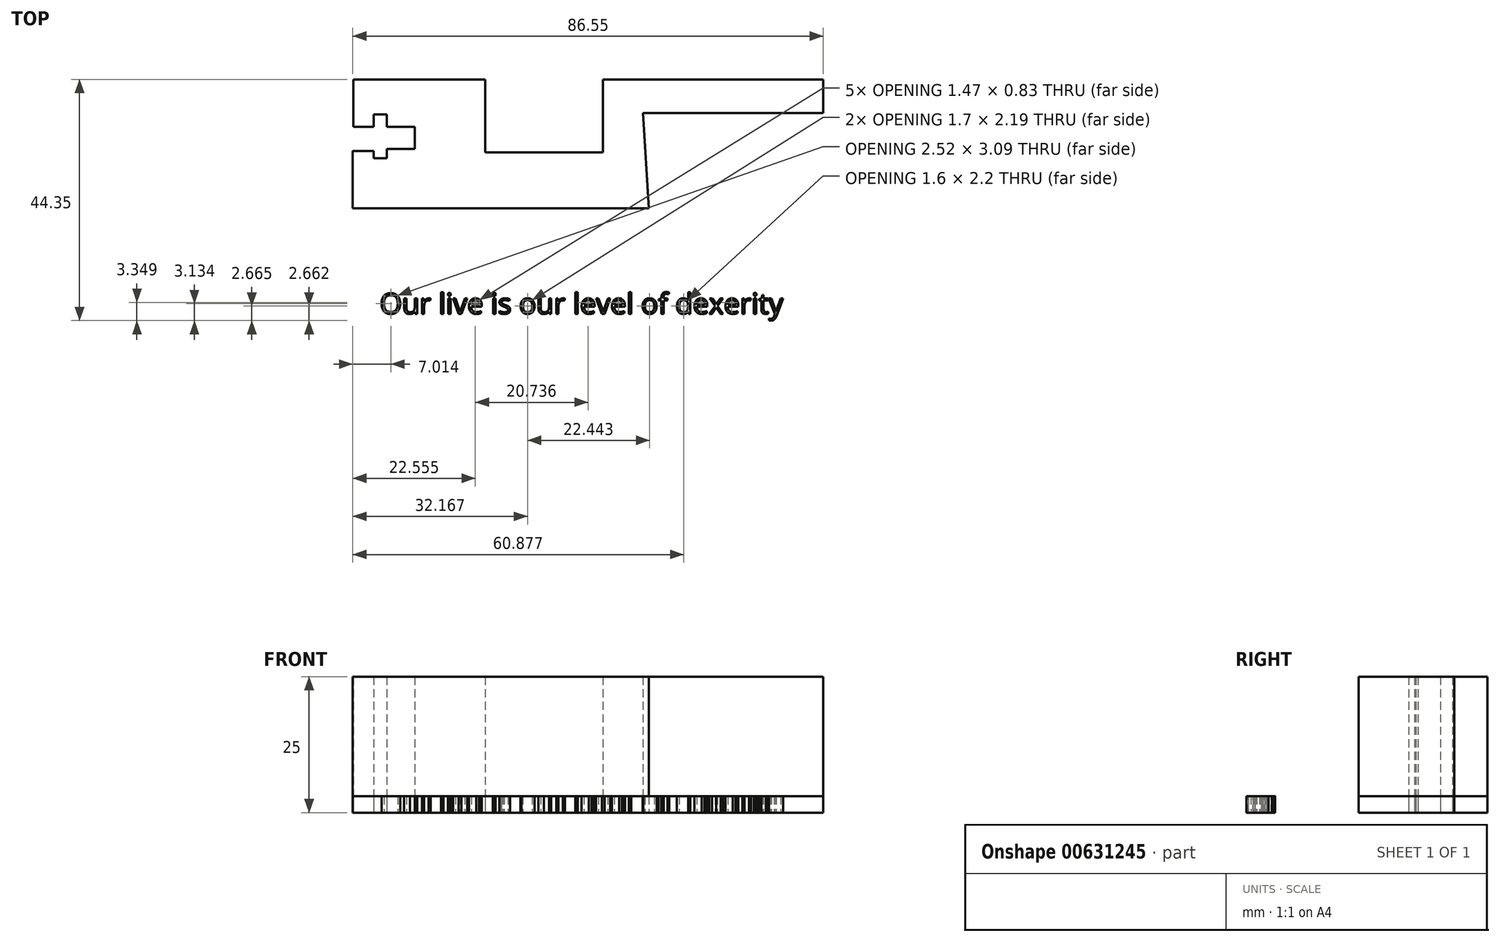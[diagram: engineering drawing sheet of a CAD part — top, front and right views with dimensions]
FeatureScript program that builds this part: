
annotation { "Feature Type Name" : "Feature", "Feature Type Description" : "" }
export const myFeature = defineFeature(function(context is Context, id is Id, definition is map)
    precondition{}
    {
        {
            var Q0;
            Q0=qCreatedBy(makeId("Top.planeOp"),FACE);
            var sketch = newSketch(context, id + "F0", { "sketchPlane" : qUnion([Q0])});
            skLineSegment(sketch, "E0", {"start": v(-137.92, 48.65) * mm, "end": v(-113.6, 48.65) * mm});
            skLineSegment(sketch, "E1", {"start": v(-113.6, 48.65) * mm, "end": v(-113.6, 35.24) * mm});
            skLineSegment(sketch, "E2", {"start": v(-113.6, 35.24) * mm, "end": v(-91.97, 35.24) * mm});
            skLineSegment(sketch, "E3", {"start": v(-91.97, 35.24) * mm, "end": v(-91.97, 48.65) * mm});
            skLineSegment(sketch, "E4", {"start": v(-91.97, 48.65) * mm, "end": v(-51.45, 48.65) * mm});
            skLineSegment(sketch, "E5", {"start": v(-51.45, 48.65) * mm, "end": v(-51.45, 42.52) * mm});
            skLineSegment(sketch, "E6", {"start": v(-51.45, 42.52) * mm, "end": v(-84.62, 42.52) * mm});
            skLineSegment(sketch, "E7", {"start": v(-84.62, 42.52) * mm, "end": v(-83.55, 24.95) * mm});
            skLineSegment(sketch, "E8", {"start": v(-83.55, 24.95) * mm, "end": v(-138, 24.95) * mm});
            skLineSegment(sketch, "E9", {"start": v(-138, 24.95) * mm, "end": v(-138, 35.48) * mm});
            skLineSegment(sketch, "E10", {"start": v(-138, 35.48) * mm, "end": v(-134.17, 35.48) * mm});
            skLineSegment(sketch, "E11", {"start": v(-134.17, 35.48) * mm, "end": v(-134.17, 34.15) * mm});
            skLineSegment(sketch, "E12", {"start": v(-134.17, 34.15) * mm, "end": v(-131.76, 34.15) * mm});
            skLineSegment(sketch, "E13", {"start": v(-131.76, 34.15) * mm, "end": v(-131.76, 35.89) * mm});
            skLineSegment(sketch, "E14", {"start": v(-131.76, 35.89) * mm, "end": v(-126.56, 35.89) * mm});
            skLineSegment(sketch, "E15", {"start": v(-126.56, 35.89) * mm, "end": v(-126.56, 39.95) * mm});
            skLineSegment(sketch, "E16", {"start": v(-126.56, 39.95) * mm, "end": v(-131.76, 39.95) * mm});
            skLineSegment(sketch, "E17", {"start": v(-131.76, 39.95) * mm, "end": v(-131.76, 42.23) * mm});
            skLineSegment(sketch, "E18", {"start": v(-131.76, 42.23) * mm, "end": v(-134.17, 42.23) * mm});
            skLineSegment(sketch, "E19", {"start": v(-134.17, 42.23) * mm, "end": v(-134.17, 39.95) * mm});
            skLineSegment(sketch, "E20", {"start": v(-134.17, 39.95) * mm, "end": v(-137.9, 39.95) * mm});
            skLineSegment(sketch, "E21", {"start": v(-137.9, 39.95) * mm, "end": v(-137.92, 48.65) * mm});
            skText(sketch, "E22", { "text": "Our live is our level of dexerity", "fontName": "OpenSans-Regular.ttf"});
            const initialGuessF0  = {"E22": [-0.13303, 0.00556, 1, 0, 0.00378]};
            skSetInitialGuess(sketch, initialGuessF0);
            skSolve(sketch);
        }
        {
            var Q0;
            Q0=makeQuery(id+"F0.imprint","IMPRINT",FACE,{"disambiguationData":[TD([[makeQuery(id+"F0.imprint","IMPRINT",EDGE,{"derivedFrom":sQuery(id+"F0.wireOp",EDGE,"E0")}),-1.0]])]});
            extrude(context, id + "F1", {"entities" : qUnion([Q0]), "depth" : 3 * mm, "offsetDistance" : 25 * mm});
        }
        {
            var Q0;
            Q0=makeQuery(id+"F0.imprint","IMPRINT",FACE,{"disambiguationData":[TD([[makeQuery(id+"F0.imprint","IMPRINT",EDGE,{"derivedFrom":sQuery(id+"F0.wireOp",EDGE,"E0")}),-1.0]])]});
            extrude(context, id + "F2", {"entities" : qUnion([Q0]), "depth" : 25 * mm, "offsetDistance" : 25 * mm});
        }
        {
            var Q0;
            Q0 = qSketchRegion(id + "F0", true);
            extrude(context, id + "F3", {"entities" : qUnion([Q0]), "depth" : 3 * mm, "offsetDistance" : 25 * mm});
        }
    });
